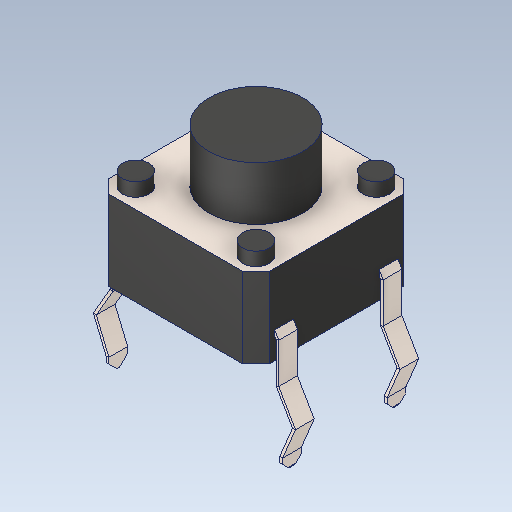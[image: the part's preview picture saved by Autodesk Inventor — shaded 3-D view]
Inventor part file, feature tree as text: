
AUTODESK INVENTOR PART (.ipt)
format: ipt  version: 2020.1 (Build 241239000, 239)  size: 188,928 bytes
history: mixed  units: mm
features: mirror x1, imported_body x1
ambient origin geometry x8: Origin, YZ Plane, XZ Plane, XY Plane, X Axis, Y Axis, Z Axis, Center Point
bodies: Solid1 (imported_parasolid)
feature tree (2):
  mirror  "Mirror3"
  imported_body  NMx_Import_Brep_tag  [imported B-rep: ~116 faces, bbox_mm=[7.565599, 8.48991, 6.01]]
